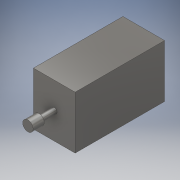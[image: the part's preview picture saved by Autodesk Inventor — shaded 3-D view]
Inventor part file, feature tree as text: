
AUTODESK INVENTOR PART (.ipt)
format: ipt  version: 2019 (Build 230136000, 136)  size: 140,800 bytes
history: native  units: mm
features: extrude x7, sketch x7
ambient origin geometry x8: Origin, YZ Plane, XZ Plane, XY Plane, X Axis, Y Axis, Z Axis, Center Point
bodies: Solid1 (feature_tree), Solid2 (feature_tree)
feature tree (14):
  extrude  "Extrusion1"  Depth=64.4mm
  extrude  "Extrusion4"  Depth=4.0mm
  extrude  "Extrusion5"  Depth=7.5mm
  extrude  "Extrusion2"  Depth=4.0mm
  extrude  "Extrusion3"  Depth=2.0mm TaperAngle=0.0deg
  extrude  "Extrusion6"  Depth=62.4mm TaperAngle=0.0deg
  extrude  "Extrusion7"  Depth=68.4mm TaperAngle=0.0deg
  sketch  "Sketch1"  dims[d0=30.0mm d1=64.4mm]
  sketch  "Sketch2"  dims[d2=38.0mm d3=0.0mm d4=4.0mm]
  sketch  "Sketch3"  dims[d5=11.0mm d6=0.0mm d7=7.5mm]
  sketch  "Sketch4"  dims[d8=8.0mm d9=0.0mm d10=4.0mm]
  sketch  "Sketch5"  dims[d11=8.0mm d12=0.0mm d13=2.0mm d14=0.0mm]
  sketch  "Sketch6"  dims[d15=15.0mm d16=62.4mm d17=0.0mm]
  sketch  "Sketch7"  dims[d18=15.0mm d19=68.4mm d20=0.0mm d21=25.0mm d22=2.0mm d23=0.0mm]
